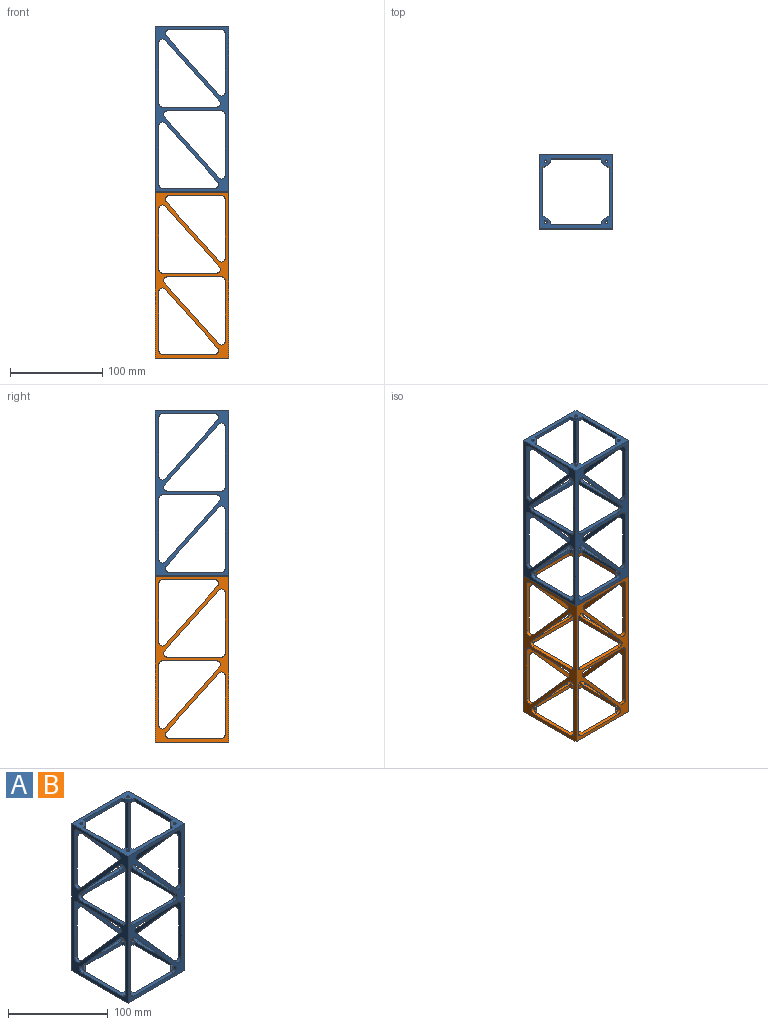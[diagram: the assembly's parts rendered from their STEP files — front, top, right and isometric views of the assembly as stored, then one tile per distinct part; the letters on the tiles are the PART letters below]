
ASSEMBLY  parts=2 mates=1
PART A: 134 faces, bbox 80x80x180 mm
  f0: cylinder r=1.5mm len=3mm, axis (0,0,-1), area 28.3mm2, adj f70,f129
  f1: cylinder r=1.5mm len=3mm, axis (0,0,-1), area 28.3mm2, adj f70,f128
  f2: cylinder r=1.5mm len=3mm, axis (0,0,-1), area 28.3mm2, adj f70,f127
  f3: cylinder r=1.5mm len=3mm, axis (0,0,-1), area 28.3mm2, adj f70,f126
  f4: plane 180x72mm, normal (0,1,0), area 2095.2mm2, adj f5,f6,f13,f16,f17,f18,f19,f20
  f5: plane 180x72mm, normal (-1,0,0), area 2095.2mm2, adj f4,f11,f12,f23,f26,f29,f33,f50
  f6: cylinder r=4mm len=4mm, axis (0,0,1), area 9.1mm2, adj f4,f26,f94
  f7: plane 180x72mm, normal (1,0,0), area 2095.2mm2, adj f9,f10,f13,f22,f27,f30,f34,f36
  f8: cylinder r=4mm len=4mm, axis (0,0,-1), area 2.5mm2, adj f27,f75,f101
  f9: plane 180x72mm, normal (0,-1,0), area 2095.2mm2, adj f7,f11,f14,f22,f47,f48,f51,f53
  f10: cylinder r=4mm len=4mm, axis (0,0,1), area 9.1mm2, adj f7,f57,f74
  f11: cylinder r=4mm len=11.2mm, axis (0,0,-1), area 65.5mm2, adj f5,f9,f78,f96,f122
  f12: cylinder r=4mm len=4mm, axis (0,0,1), area 9.1mm2, adj f5,f23,f52
  f13: cylinder r=4mm len=11.2mm, axis (0,0,-1), area 65.5mm2, adj f4,f7,f20,f38,f117
  f14: cylinder r=4mm len=4mm, axis (0,0,1), area 9.1mm2, adj f9,f22,f87
  f15: cylinder r=4mm len=4mm, axis (0,0,-1), area 2.5mm2, adj f71,f73,f103
  f16: plane 63.97x56.86mm, normal (0.75,0,0.66), area 342.3mm2, adj f4,f24,f50,f68
  f17: cylinder r=4mm len=6.99mm, axis (0,-1,0), area 41.1mm2, adj f4,f25,f44,f54,f68,f108
  f18: plane 65.97x58.64mm, normal (0.75,0,0.66), area 353.1mm2, adj f4,f32,f61,f68
  f19: plane 65.97x58.64mm, normal (-0.75,0,-0.66), area 353.1mm2, adj f4,f20,f21,f68
  f20: cylinder r=4mm len=6.99mm, axis (0,-1,0), area 41.1mm2, adj f4,f13,f19,f38,f63,f68
  f21: cylinder r=4mm len=6.66mm, axis (0,1,0), area 36.8mm2, adj f4,f19,f35,f68
  f22: plane 60.86x13.42mm, normal (0,0,-1), area 263.9mm2, adj f7,f9,f14,f37,f47,f87,f114,f132
  f23: plane 60.86x13.42mm, normal (0,0,-1), area 263.9mm2, adj f4,f5,f12,f24,f52,f68,f119,f130
  f24: cylinder r=4mm len=6.66mm, axis (0,1,0), area 36.8mm2, adj f4,f16,f23,f68
  f25: plane 63.97x56.86mm, normal (-0.75,0,-0.66), area 342.3mm2, adj f4,f17,f28,f68
  f26: plane 60.86x13.42mm, normal (0,0,1), area 263.9mm2, adj f4,f5,f6,f46,f94,f95,f125,f126
  f27: plane 64.86x64.86mm, normal (0,0,1), area 491.3mm2, adj f4,f7,f8,f28,f43,f47,f68,f75
  f28: cylinder r=4mm len=6.66mm, axis (0,1,0), area 36.8mm2, adj f4,f25,f27,f68
  f29: plane 58.64x4mm, normal (0,0,-1), area 234.6mm2, adj f5,f46,f97,f100
  f30: plane 58.64x4mm, normal (0,0,-1), area 234.6mm2, adj f7,f41,f47,f90
  f31: plane 58.64x4mm, normal (0,0,-1), area 234.6mm2, adj f4,f32,f68,f77
  f32: cylinder r=4mm len=6.66mm, axis (0,-1,0), area 36.8mm2, adj f4,f18,f31,f68
  f33: plane 58.64x4mm, normal (0,0,1), area 234.6mm2, adj f5,f46,f82,f83
  f34: plane 58.64x4mm, normal (0,0,1), area 234.6mm2, adj f7,f40,f47,f89
  f35: plane 58.64x4mm, normal (0,0,1), area 234.6mm2, adj f4,f21,f65,f68
  f36: plane 63.97x56.86mm, normal (0,0.75,0.66), area 342.3mm2, adj f7,f37,f47,f86
  f37: cylinder r=4mm len=6.66mm, axis (-1,0,0), area 36.8mm2, adj f7,f22,f36,f47
  f38: cylinder r=4mm len=6.99mm, axis (1,0,0), area 41.1mm2, adj f7,f13,f20,f39,f47,f88
  f39: plane 65.97x58.64mm, normal (0,-0.75,-0.66), area 353.1mm2, adj f7,f38,f40,f47
  f40: cylinder r=4mm len=6.66mm, axis (-1,0,0), area 36.8mm2, adj f7,f34,f39,f47
  f41: cylinder r=4mm len=6.66mm, axis (-1,0,0), area 36.8mm2, adj f7,f30,f42,f47
  f42: plane 65.97x58.64mm, normal (0,0.75,0.66), area 353.1mm2, adj f7,f41,f47,f91
  f43: cylinder r=4mm len=6.66mm, axis (-1,0,0), area 36.8mm2, adj f7,f27,f45,f47
  f44: cylinder r=4mm len=6.99mm, axis (1,0,0), area 41.1mm2, adj f7,f17,f45,f47,f102,f108
  f45: plane 63.97x56.86mm, normal (0,-0.75,-0.66), area 342.3mm2, adj f7,f43,f44,f47
  f46: plane 180x80mm, normal (1,0,0), area 3339mm2, adj f4,f26,f29,f33,f67,f68,f69,f70
  f47: plane 180x80mm, normal (-1,0,0), area 3339mm2, adj f9,f22,f27,f30,f34,f36,f37,f38
  f48: plane 63.97x56.86mm, normal (0.75,0,0.66), area 342.3mm2, adj f9,f51,f67,f72
  f49: plane 63.97x4mm, normal (-1,0,0), area 255.9mm2, adj f67,f72,f73,f105
  f50: cylinder r=4mm len=6.99mm, axis (0,-1,0), area 38.6mm2, adj f4,f5,f16,f68
  f51: cylinder r=4mm len=6.66mm, axis (0,1,0), area 36.8mm2, adj f9,f48,f67,f71
  f52: cylinder r=4mm len=8mm, axis (0,-1,0), area 34.3mm2, adj f5,f12,f23,f68
  f53: plane 63.97x56.86mm, normal (-0.75,0,-0.66), area 342.3mm2, adj f9,f55,f56,f67
  f54: plane 63.97x4mm, normal (1,0,0), area 255.9mm2, adj f17,f68,f75,f102
  f55: cylinder r=4mm len=6.66mm, axis (0,1,0), area 36.8mm2, adj f9,f53,f67,f74
  f56: cylinder r=4mm len=6.99mm, axis (0,-1,0), area 38.6mm2, adj f7,f9,f53,f67
  f57: cylinder r=4mm len=8mm, axis (0,-1,0), area 34.3mm2, adj f7,f10,f67,f74
  f58: plane 65.97x58.64mm, normal (0.75,0,0.66), area 353.1mm2, adj f9,f62,f67,f78
  f59: plane 65.97x4mm, normal (-1,0,0), area 263.9mm2, adj f60,f67,f78,f98
  f60: cylinder r=4mm len=5.17mm, axis (0,1,0), area 27.6mm2, adj f59,f67,f76,f97,f110
  f61: cylinder r=4mm len=6.99mm, axis (0,-1,0), area 38.6mm2, adj f4,f5,f18,f68
  f62: cylinder r=4mm len=6.66mm, axis (0,-1,0), area 36.8mm2, adj f9,f58,f67,f76
  f63: plane 65.97x4mm, normal (1,0,0), area 263.9mm2, adj f20,f65,f68,f88
  f64: plane 65.97x58.64mm, normal (-0.75,0,-0.66), area 353.1mm2, adj f9,f66,f67,f81
  f65: cylinder r=4mm len=5.17mm, axis (0,1,0), area 27.6mm2, adj f35,f63,f68,f89,f108
  f66: cylinder r=4mm len=6.99mm, axis (0,-1,0), area 38.6mm2, adj f7,f9,f64,f67
  f67: plane 180x80mm, normal (0,1,0), area 3339mm2, adj f7,f46,f47,f48,f49,f51,f53,f55
  f68: plane 180x80mm, normal (0,-1,0), area 3339mm2, adj f5,f16,f17,f18,f19,f20,f21,f23
  f69: plane 80x80mm, normal (0,0,1), area 1425.6mm2, adj f4,f5,f7,f9,f46,f47,f67,f68
  f70: plane 80x80mm, normal (0,0,-1), area 1425.6mm2, adj f0,f1,f2,f3,f4,f5,f7,f9
  f71: plane 64.86x64.86mm, normal (0,0,-1), area 491.3mm2, adj f5,f9,f15,f46,f51,f67,f73,f103
  f72: cylinder r=4mm len=6.99mm, axis (0,-1,0), area 41.1mm2, adj f9,f48,f49,f67,f104,f110
  f73: cylinder r=4mm len=5.17mm, axis (0,-1,0), area 27.6mm2, adj f15,f49,f67,f71,f103
  f74: plane 60.86x13.42mm, normal (0,0,1), area 263.9mm2, adj f7,f9,f10,f55,f57,f67,f123,f128
  f75: cylinder r=4mm len=5.17mm, axis (0,-1,0), area 27.6mm2, adj f8,f27,f54,f68,f101
  f76: plane 58.64x4mm, normal (0,0,-1), area 234.6mm2, adj f9,f60,f62,f67
  f77: cylinder r=4mm len=8mm, axis (0,1,0), area 34.3mm2, adj f5,f31,f68,f111
  f78: cylinder r=4mm len=6.99mm, axis (0,-1,0), area 41.1mm2, adj f9,f11,f58,f59,f67,f96
  f79: plane 58.64x4mm, normal (0,0,1), area 234.6mm2, adj f9,f67,f80,f81
  f80: cylinder r=4mm len=8mm, axis (0,1,0), area 34.3mm2, adj f7,f67,f79,f109
  f81: cylinder r=4mm len=6.66mm, axis (0,1,0), area 36.8mm2, adj f9,f64,f67,f79
  f82: cylinder r=4mm len=8mm, axis (-1,0,0), area 34.3mm2, adj f4,f33,f46,f111
  f83: cylinder r=4mm len=6.66mm, axis (-1,0,0), area 36.8mm2, adj f5,f33,f46,f84
  f84: plane 65.97x58.64mm, normal (0,-0.75,-0.66), area 353.1mm2, adj f5,f46,f83,f85
  f85: cylinder r=4mm len=6.99mm, axis (1,0,0), area 38.6mm2, adj f4,f5,f46,f84
  f86: cylinder r=4mm len=6.99mm, axis (1,0,0), area 38.6mm2, adj f7,f9,f36,f47
  f87: cylinder r=4mm len=8mm, axis (-1,0,0), area 34.3mm2, adj f9,f14,f22,f47
  f88: plane 65.97x4mm, normal (0,1,0), area 263.9mm2, adj f38,f47,f63,f89
  f89: cylinder r=4mm len=5.17mm, axis (-1,0,0), area 27.6mm2, adj f34,f47,f65,f88,f108
  f90: cylinder r=4mm len=8mm, axis (-1,0,0), area 34.3mm2, adj f9,f30,f47,f109
  f91: cylinder r=4mm len=6.99mm, axis (1,0,0), area 38.6mm2, adj f7,f9,f42,f47
  f92: plane 63.97x56.86mm, normal (0,-0.75,-0.66), area 342.3mm2, adj f5,f46,f93,f95
  f93: cylinder r=4mm len=6.99mm, axis (1,0,0), area 38.6mm2, adj f4,f5,f46,f92
  f94: cylinder r=4mm len=8mm, axis (-1,0,0), area 34.3mm2, adj f4,f6,f26,f46
  f95: cylinder r=4mm len=6.66mm, axis (-1,0,0), area 36.8mm2, adj f5,f26,f46,f92
  f96: cylinder r=4mm len=6.99mm, axis (1,0,0), area 41.1mm2, adj f5,f11,f46,f78,f98,f99
  f97: cylinder r=4mm len=5.17mm, axis (-1,0,0), area 27.6mm2, adj f29,f46,f60,f98,f110
  f98: plane 65.97x4mm, normal (0,-1,0), area 263.9mm2, adj f46,f59,f96,f97
  f99: plane 65.97x58.64mm, normal (0,0.75,0.66), area 353.1mm2, adj f5,f46,f96,f100
  f100: cylinder r=4mm len=6.66mm, axis (-1,0,0), area 36.8mm2, adj f5,f29,f46,f99
  f101: cylinder r=4mm len=5.17mm, axis (-1,0,0), area 27.6mm2, adj f8,f27,f47,f75,f102
  f102: plane 63.97x4mm, normal (0,1,0), area 255.9mm2, adj f44,f47,f54,f101
  f103: cylinder r=4mm len=5.17mm, axis (-1,0,0), area 27.6mm2, adj f15,f46,f71,f73,f105
  f104: cylinder r=4mm len=6.99mm, axis (1,0,0), area 41.1mm2, adj f5,f46,f72,f105,f106,f110
  f105: plane 63.97x4mm, normal (0,-1,0), area 255.9mm2, adj f46,f49,f103,f104
  f106: plane 63.97x56.86mm, normal (0,0.75,0.66), area 342.3mm2, adj f5,f46,f104,f107
  f107: cylinder r=4mm len=6.66mm, axis (-1,0,0), area 36.8mm2, adj f5,f46,f71,f106
  f108: cylinder r=4mm len=18.37mm, axis (0,0,-1), area 105.7mm2, adj f4,f7,f17,f44,f65,f89
  f109: cylinder r=4mm len=12mm, axis (0,0,1), area 43.4mm2, adj f7,f9,f80,f90
  f110: cylinder r=4mm len=18.37mm, axis (0,0,-1), area 105.7mm2, adj f5,f9,f60,f72,f97,f104
  f111: cylinder r=4mm len=12mm, axis (0,0,1), area 43.4mm2, adj f4,f5,f77,f82
  f112: cylinder r=14mm len=9.42mm, axis (0,0,1), area 55.5mm2, adj f5,f9,f69,f71
  f113: cylinder r=1.5mm len=3mm, axis (0,0,1), area 28.3mm2, adj f69,f133
  f114: cylinder r=14mm len=9.42mm, axis (0,0,1), area 55.5mm2, adj f7,f9,f22,f69
  f115: cylinder r=1.5mm len=3mm, axis (0,0,1), area 28.3mm2, adj f69,f132
  f116: cylinder r=14mm len=9.42mm, axis (0,0,1), area 55.5mm2, adj f4,f7,f69,f117
  f117: plane 9.42x9.42mm, normal (0,0,-1), area 36.4mm2, adj f4,f7,f13,f116,f131
  f118: cylinder r=1.5mm len=3mm, axis (0,0,1), area 28.3mm2, adj f69,f131
  f119: cylinder r=14mm len=9.42mm, axis (0,0,1), area 55.5mm2, adj f4,f5,f23,f69
  f120: cylinder r=1.5mm len=3mm, axis (0,0,1), area 28.3mm2, adj f69,f130
  f121: cylinder r=14mm len=9.42mm, axis (0,0,-1), area 55.5mm2, adj f5,f9,f70,f122
  f122: plane 9.42x9.42mm, normal (0,0,1), area 36.4mm2, adj f5,f9,f11,f121,f129
  f123: cylinder r=14mm len=9.42mm, axis (0,0,-1), area 55.5mm2, adj f7,f9,f70,f74
  f124: cylinder r=14mm len=9.42mm, axis (0,0,-1), area 55.5mm2, adj f4,f7,f27,f70
  f125: cylinder r=14mm len=9.42mm, axis (0,0,-1), area 55.5mm2, adj f4,f5,f26,f70
  f126: cone r=1.5mm half-angle=45deg, axis (0,0,1), area 17.8mm2, adj f3,f26
  f127: cone r=1.5mm half-angle=45deg, axis (0,0,1), area 17.8mm2, adj f2,f27
  f128: cone r=1.5mm half-angle=45deg, axis (0,0,1), area 17.8mm2, adj f1,f74
  f129: cone r=1.5mm half-angle=45deg, axis (0,0,1), area 17.8mm2, adj f0,f122
  f130: cone r=1.5mm half-angle=45deg, axis (0,0,-1), area 17.8mm2, adj f23,f120
  f131: cone r=1.5mm half-angle=45deg, axis (0,0,-1), area 17.8mm2, adj f117,f118
  f132: cone r=1.5mm half-angle=45deg, axis (0,0,-1), area 17.8mm2, adj f22,f115
  f133: cone r=1.5mm half-angle=45deg, axis (0,0,-1), area 17.8mm2, adj f71,f113
PART B: same geometry as A
PLACE A t=(8.25,-3.17,162.73)mm
PLACE B t=(8.25,-3.17,-17.27)mm
MATE fastened A.f118 <-> B.f2  axis (0,0,-1) through (-24.68,-36.1,162.73)mm
